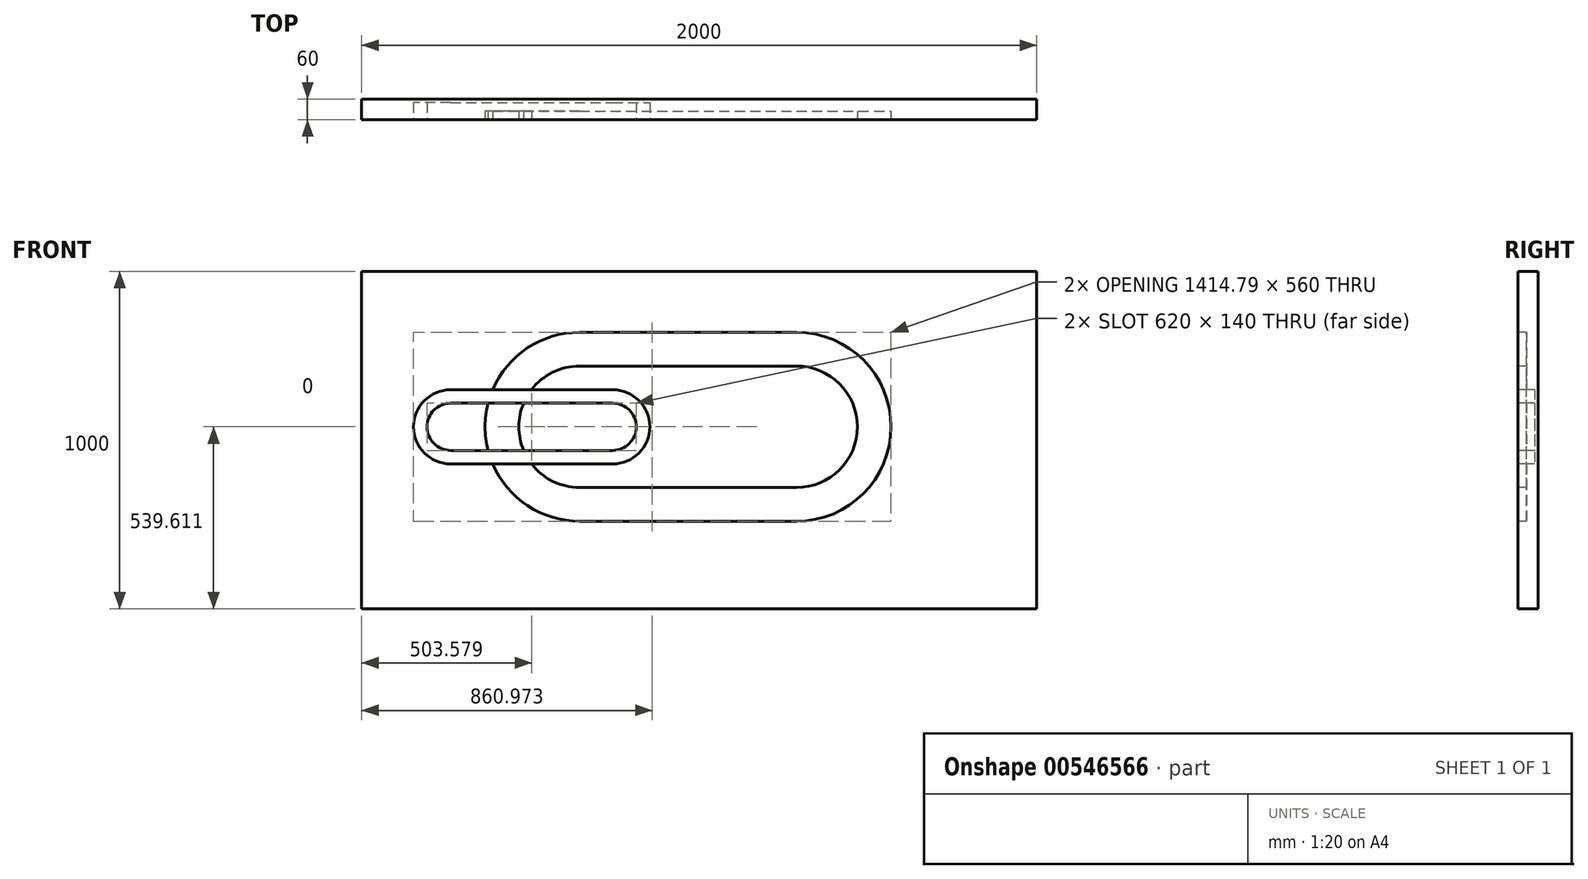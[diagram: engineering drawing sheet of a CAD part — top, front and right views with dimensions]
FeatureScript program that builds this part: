
annotation { "Feature Type Name" : "Feature", "Feature Type Description" : "" }
export const myFeature = defineFeature(function(context is Context, id is Id, definition is map)
    precondition{}
    {
        {
            var Q0;
            Q0=qCreatedBy(makeId("Front.planeOp"),FACE);
            var sketch = newSketch(context, id + "F0", { "sketchPlane" : qUnion([Q0])});
            skLineSegment(sketch, "E0.bottom", {"start": v(-1239.96, 655.47) * mm, "end": v(760.04, 655.47) * mm});
            skLineSegment(sketch, "E0.top", {"start": v(-1239.96, -344.53) * mm, "end": v(760.04, -344.53) * mm});
            skLineSegment(sketch, "E0.left", {"start": v(-1239.96, 655.47) * mm, "end": v(-1239.96, -344.53) * mm});
            skLineSegment(sketch, "E0.right", {"start": v(760.04, 655.47) * mm, "end": v(760.04, -344.53) * mm});
            skSolve(sketch);
        }
        {
            var Q0;
            Q0=makeQuery(id+"F0.imprint","IMPRINT",FACE,{"disambiguationData":[TD([[makeQuery(id+"F0.imprint","IMPRINT",EDGE,{"derivedFrom":sQuery(id+"F0.wireOp",EDGE,"E0.bottom")}),-1.0]])]});
            extrude(context, id + "F1", {"entities" : qUnion([Q0]), "depth" : 60 * mm, "offsetDistance" : 25 * mm});
        }
        {
            var Q0;
            Q0=makeQuery(id+"F1.opExtrude","CAP_FACE",FACE,{"disambiguationData":[OSD([sQuery(id+"F0.wireOp",EDGE,"E0.bottom"),sQuery(id+"F0.wireOp",EDGE,"E0.top"),sQuery(id+"F0.wireOp",EDGE,"E0.left"),sQuery(id+"F0.wireOp",EDGE,"E0.right")])],"isStart":false});
            var sketch = newSketch(context, id + "F2", { "sketchPlane" : qUnion([Q0])});
            skArc(sketch, "E1", {"start": v(-976.38, 305.08) * mm, "mid": v(-1086.38, 195.08) * mm, "end": v(-976.38, 85.08) * mm});
            skArc(sketch, "E2", {"start": v(-496.38, 85.08) * mm, "mid": v(-386.38, 195.08) * mm, "end": v(-496.38, 305.08) * mm});
            skLineSegment(sketch, "E3", {"start": v(-976.38, 305.08) * mm, "end": v(-496.38, 305.08) * mm});
            skLineSegment(sketch, "E4", {"start": v(-976.38, 85.08) * mm, "end": v(-496.38, 85.08) * mm});
            skArc(sketch, "E5.0", {"start": v(-976.38, 265.08) * mm, "mid": v(-1046.38, 195.08) * mm, "end": v(-976.38, 125.08) * mm});
            skLineSegment(sketch, "E5.1", {"start": v(-976.38, 265.08) * mm, "end": v(-496.38, 265.08) * mm});
            skArc(sketch, "E5.2", {"start": v(-496.38, 125.08) * mm, "mid": v(-426.38, 195.08) * mm, "end": v(-496.38, 265.08) * mm});
            skLineSegment(sketch, "E5.3", {"start": v(-976.38, 125.08) * mm, "end": v(-496.38, 125.08) * mm});
            skLineSegment(sketch, "E6.0", {"start": v(-1244.96, 660.47) * mm, "end": v(-1244.96, -349.53) * mm});
            skLineSegment(sketch, "E6.1", {"start": v(765.04, 660.47) * mm, "end": v(-1244.96, 660.47) * mm});
            skLineSegment(sketch, "E6.2", {"start": v(765.04, -349.53) * mm, "end": v(765.04, 660.47) * mm});
            skLineSegment(sketch, "E6.3", {"start": v(-1244.96, -349.53) * mm, "end": v(765.04, -349.53) * mm});
            skSolve(sketch);
        }
        {
            var Q0;
            Q0=makeQuery(id+"F2.imprint","IMPRINT",FACE,{"disambiguationData":[TD([[makeQuery(id+"F2.imprint","IMPRINT",EDGE,{"derivedFrom":sQuery(id+"F2.wireOp",EDGE,"E1")}),1.0]])]});
            extrude(context, id + "F3", {"entities" : qUnion([Q0]), "operationType" : NewBodyOperationType.REMOVE, "oppositeDirection" : true, "depth" : 50 * mm, "offsetDistance" : 25 * mm});
        }
        {
            var Q0;
            {var subQ0=sQuery(id+"F0.wireOp",EDGE,"E0.left");var subQ1=sQuery(id+"F0.wireOp",EDGE,"E0.top");var subQ2=sQuery(id+"F0.wireOp",EDGE,"E0.right");var subQ3=sQuery(id+"F0.wireOp",EDGE,"E0.bottom");Q0=makeQuery(id+"F3.boolean.opBoolean","SPLIT",FACE,{"disambiguationData":[TD([makeQuery(id+"F1.opExtrude","SWEPT_FACE",FACE,{"disambiguationData":[OSD([subQ3])]})])],"derivedFrom":makeQuery(id+"F1.opExtrude","CAP_FACE",FACE,{"disambiguationData":[OSD([subQ3,subQ1,subQ0,subQ2])],"isStart":false})});}
            var sketch = newSketch(context, id + "F4", { "sketchPlane" : qUnion([Q0])});
            skArc(sketch, "E7", {"start": v(-594.35, 375.08) * mm, "mid": v(-774.35, 195.08) * mm, "end": v(-594.35, 15.08) * mm});
            skPoint(sketch, "E7.centerSnap0", {"position": v(-1086.38, 195.08) * mm});
            skArc(sketch, "E8", {"start": v(48.4, 15.08) * mm, "mid": v(228.4, 195.08) * mm, "end": v(48.4, 375.08) * mm});
            skPoint(sketch, "E8.centerSnap0", {"position": v(-386.38, 195.08) * mm});
            skLineSegment(sketch, "E9", {"start": v(-594.35, 375.08) * mm, "end": v(48.4, 375.08) * mm});
            skLineSegment(sketch, "E10", {"start": v(-594.35, 15.08) * mm, "end": v(48.4, 15.08) * mm});
            skArc(sketch, "E11.0", {"start": v(-594.35, 475.08) * mm, "mid": v(-874.35, 195.08) * mm, "end": v(-594.35, -84.92) * mm});
            skLineSegment(sketch, "E11.1", {"start": v(-594.35, 475.08) * mm, "end": v(48.4, 475.08) * mm});
            skArc(sketch, "E11.2", {"start": v(48.4, -84.92) * mm, "mid": v(328.4, 195.08) * mm, "end": v(48.4, 475.08) * mm});
            skLineSegment(sketch, "E11.3", {"start": v(-594.35, -84.92) * mm, "end": v(48.4, -84.92) * mm});
            skSolve(sketch);
        }
        {
            var Q0;
            Q0=makeQuery(id+"F4.imprint","IMPRINT",FACE,{"disambiguationData":[TD([[makeQuery(id+"F4.imprint","IMPRINT",EDGE,{"derivedFrom":sQuery(id+"F4.wireOp",EDGE,"E8")}),-1.0]])]});
            var Q1;
            {var subQ0=sQuery(id+"F4.wireOp",EDGE,"E7");var subQ1=makeQuery(id+"F3.boolean.opBoolean","COPY",EDGE,{"derivedFrom":makeQuery(id+"F3.opExtrude","CAP_EDGE",EDGE,{"disambiguationData":[OSD([sQuery(id+"F2.wireOp",EDGE,"E3")])],"isStart":true})});var subQ2=makeQuery(id+"F4.imprint","INTERSECT",VERTEX,{"derivedFrom":[subQ1,subQ0]});Q1=makeQuery(id+"F4.imprint","IMPRINT",FACE,{"disambiguationData":[TD([[makeQuery(id+"F4.imprint","IMPRINT",EDGE,{"disambiguationData":[TD([[subQ2,-1.0]])],"derivedFrom":subQ0}),-1.0]])]});}
            extrude(context, id + "F5", {"entities" : qUnion([Q0, Q1]), "operationType" : NewBodyOperationType.REMOVE, "oppositeDirection" : true, "depth" : 25 * mm, "offsetDistance" : 25 * mm});
        }
    });
